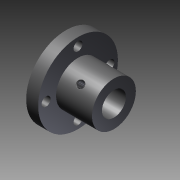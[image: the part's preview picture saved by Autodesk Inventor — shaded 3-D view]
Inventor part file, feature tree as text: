
AUTODESK INVENTOR PART (.ipt)
format: ipt  version: 2016 (Build 200138000, 138)  size: 144,896 bytes
history: native  units: mm
features: sketch x4, revolve x3, thread x2, hole x1, pattern_linear x1
ambient origin geometry x8: Origin, YZ Plane, XZ Plane, XY Plane, X Axis, Y Axis, Z Axis, Center Point
bodies: Solid1 (feature_tree)
feature tree (11):
  revolve  "Revolution1"  [1 undecoded]
  hole  "Hole1"  [1 undecoded]
  pattern_linear  "Rectangular Pattern1"  Spacing1=4.96415mm  [1 undecoded]
  revolve  "Revolution2"  [1 undecoded]
  thread  "Thread1"  [1 undecoded]
  revolve  "Revolution3"  [1 undecoded]
  thread  "Thread2"  [1 undecoded]
  sketch  "Sketch_1"  dims[d0=360.0deg]
  sketch  "Sketch2"  dims[d1=4.5mm d2=6.0mm d3=4.0mm d4=2.0mm d5=90.0deg d6=6.0mm d7=0.0mm d8=20.0mm d10=22.627417mm d11=20.0mm d13=22.627417mm]
  sketch  "Sketch_4"  dims[d14=360.0deg d15=4.96415mm d16=0.0mm]
  sketch  "Sketch_5"  dims[d17=360.0deg d18=4.96415mm d19=0.0mm]
note: 7 required parameter values undecoded (feature->parameter linkage not recoverable at this tier; creation-order binding heuristic only, values carry confidence <= 0.55)